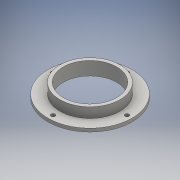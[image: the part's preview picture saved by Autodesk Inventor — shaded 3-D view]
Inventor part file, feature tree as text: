
AUTODESK INVENTOR PART (.ipt)
format: ipt  version: 2016 (Build 200138000, 138)  size: 126,976 bytes
history: native  units: mm
features: extrude x3, sketch x3, other x1, pattern_circular x1
ambient origin geometry x8: Origin, YZ Plane, XZ Plane, XY Plane, X Axis, Y Axis, Z Axis, Center Point
bodies: Body1 (feature_tree)
feature tree (8):
  other  "Sólido1"
  extrude  "Extrusión1"  Depth=3.0mm
  extrude  "Extrusión2"  Depth=9.0mm
  extrude  "Extrusión5"  Depth=10.0mm
  pattern_circular  "Patrón circular1"  [2 undecoded]
  sketch  "Boceto1"  dims[d0=47.7mm d1=3.0mm]
  sketch  "Boceto2"  dims[d2=9.0mm d3=0.0mm d4=75.0mm]
  sketch  "Boceto6"  dims[d5=3.0mm d6=0.0mm d19=3.6mm d20=33.0mm d21=10.0mm d22=0.0mm d23=40.0mm d24=360.0deg]
note: 2 required parameter values undecoded (feature->parameter linkage not recoverable at this tier; creation-order binding heuristic only, values carry confidence <= 0.55)
